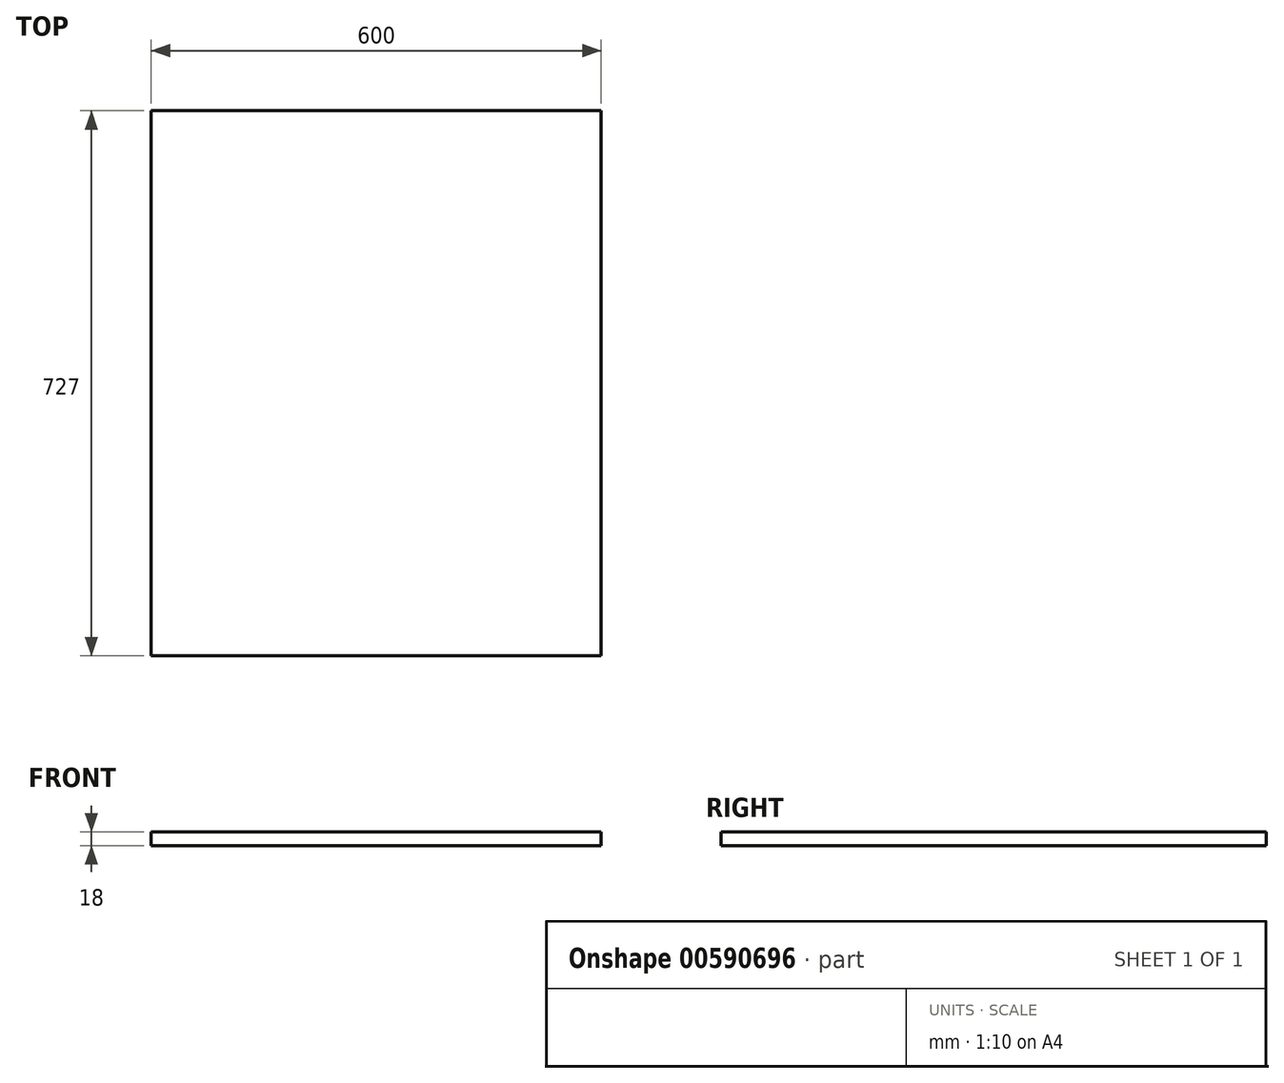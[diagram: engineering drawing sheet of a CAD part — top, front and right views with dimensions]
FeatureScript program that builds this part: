
annotation { "Feature Type Name" : "Feature", "Feature Type Description" : "" }
export const myFeature = defineFeature(function(context is Context, id is Id, definition is map)
    precondition{}
    {
        {
            assignVariable(context, id + "F0", {"name" : "longueur", "anyValue" : 745 - 18});
        }
        {
            var Q0;
            Q0=qCreatedBy(makeId("Front.planeOp"),FACE);
            var sketch = newSketch(context, id + "F1", { "sketchPlane" : qUnion([Q0])});
            skLineSegment(sketch, "E0.bottom", {"start": v(-300, 9) * mm, "end": v(300, 9) * mm});
            skLineSegment(sketch, "E0.top", {"start": v(-300, -9) * mm, "end": v(300, -9) * mm});
            skLineSegment(sketch, "E0.left", {"start": v(-300, 9) * mm, "end": v(-300, -9) * mm});
            skLineSegment(sketch, "E0.right", {"start": v(300, 9) * mm, "end": v(300, -9) * mm});
            skPoint(sketch, "E0.middle", {"position": v(0, 0) * mm});
            skSolve(sketch);
        }
        {
            var Q0;
            Q0=qSketchRegion(id+"F1",true);
            extrude(context, id + "F2", {"entities" : qUnion([Q0]), "endBound" : BoundingType.SYMMETRIC, "depth" : (getVariable(context, 'longueur')) * mm, "offsetDistance" : 25 * mm});
        }
    });
